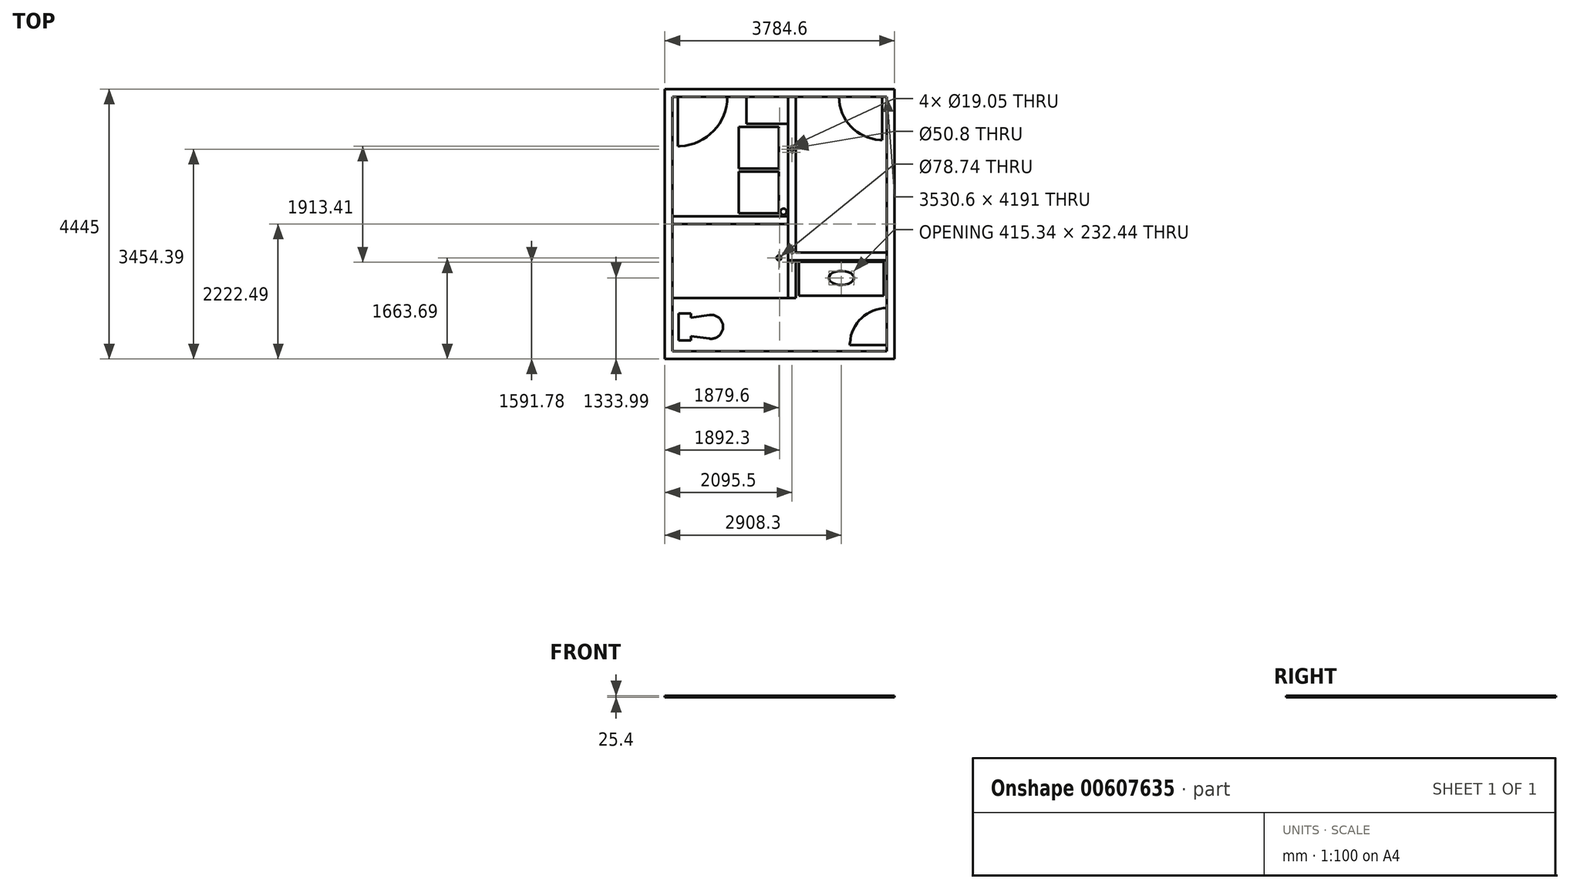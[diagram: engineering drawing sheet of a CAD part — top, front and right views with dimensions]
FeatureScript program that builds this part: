
annotation { "Feature Type Name" : "Feature", "Feature Type Description" : "" }
export const myFeature = defineFeature(function(context is Context, id is Id, definition is map)
    precondition{}
    {
        {
            var Q0;
            Q0=qCreatedBy(makeId("Top.planeOp"),FACE);
            var sketch = newSketch(context, id + "F0", { "sketchPlane" : qUnion([Q0])});
            skLineSegment(sketch, "E0.bottom", {"start": v(-1822.2, 1899.12) * mm, "end": v(1708.4, 1899.12) * mm, "construction": true});
            skLineSegment(sketch, "E0.top", {"start": v(-1822.2, -2291.88) * mm, "end": v(1708.4, -2291.88) * mm, "construction": true});
            skLineSegment(sketch, "E0.left", {"start": v(-1822.2, 1899.12) * mm, "end": v(-1822.2, -2291.88) * mm, "construction": true});
            skLineSegment(sketch, "E0.right", {"start": v(1708.4, 1899.12) * mm, "end": v(1708.4, -2291.88) * mm, "construction": true});
            skLineSegment(sketch, "E1.bottom", {"start": v(-1822.2, 1899.12) * mm, "end": v(1708.4, 1899.12) * mm});
            skLineSegment(sketch, "E1.top", {"start": v(-1822.2, -2291.88) * mm, "end": v(1708.4, -2291.88) * mm});
            skLineSegment(sketch, "E1.left", {"start": v(-1822.2, 1899.12) * mm, "end": v(-1822.2, -2291.88) * mm});
            skLineSegment(sketch, "E1.right", {"start": v(1708.4, 1899.12) * mm, "end": v(1708.4, -2291.88) * mm});
            skLineSegment(sketch, "E2", {"start": v(-1949.2, 2026.12) * mm, "end": v(1835.4, 2026.12) * mm});
            skLineSegment(sketch, "E3", {"start": v(1835.4, 2026.12) * mm, "end": v(1835.4, -2418.88) * mm});
            skLineSegment(sketch, "E4", {"start": v(1835.4, -2418.88) * mm, "end": v(-1949.2, -2418.88) * mm});
            skLineSegment(sketch, "E5", {"start": v(-1949.2, -2418.88) * mm, "end": v(-1949.2, 2026.12) * mm});
            skSolve(sketch);
        }
        {
            var Q0;
            Q0=qCreatedBy(makeId("Top.planeOp"),FACE);
            var sketch = newSketch(context, id + "F1", { "sketchPlane" : qUnion([Q0])});
            skLineSegment(sketch, "E6.bottom", {"start": v(-603, 1899.12) * mm, "end": v(82.8, 1899.12) * mm});
            skLineSegment(sketch, "E6.top", {"start": v(-603, 1454.62) * mm, "end": v(82.8, 1454.62) * mm});
            skLineSegment(sketch, "E6.left", {"start": v(-603, 1899.12) * mm, "end": v(-603, 1454.62) * mm});
            skLineSegment(sketch, "E6.right", {"start": v(82.8, 1899.12) * mm, "end": v(82.8, 1454.62) * mm});
            skSolve(sketch);
        }
        {
            var Q0;
            Q0=qCreatedBy(makeId("Top.planeOp"),FACE);
            var sketch = newSketch(context, id + "F2", { "sketchPlane" : qUnion([Q0])});
            skLineSegment(sketch, "E7.bottom", {"start": v(1708.4, -793.28) * mm, "end": v(82.8, -793.28) * mm});
            skLineSegment(sketch, "E7.top", {"start": v(1708.4, -666.28) * mm, "end": v(82.8, -666.28) * mm});
            skLineSegment(sketch, "E7.left", {"start": v(1708.4, -793.28) * mm, "end": v(1708.4, -666.28) * mm});
            skLineSegment(sketch, "E7.right", {"start": v(82.8, -793.28) * mm, "end": v(82.8, -666.28) * mm});
            skLineSegment(sketch, "E8.bottom", {"start": v(82.8, -666.28) * mm, "end": v(209.8, -666.28) * mm});
            skLineSegment(sketch, "E8.top", {"start": v(82.8, 1899.12) * mm, "end": v(209.8, 1899.12) * mm});
            skLineSegment(sketch, "E8.left", {"start": v(82.8, -666.28) * mm, "end": v(82.8, 1899.12) * mm});
            skLineSegment(sketch, "E8.right", {"start": v(209.8, -666.28) * mm, "end": v(209.8, 1899.12) * mm});
            skSolve(sketch);
        }
        {
            var Q0;
            Q0=qCreatedBy(makeId("Top.planeOp"),FACE);
            var sketch = newSketch(context, id + "F3", { "sketchPlane" : qUnion([Q0])});
            skLineSegment(sketch, "E9.bottom", {"start": v(1098.8, -2152.18) * mm, "end": v(1708.4, -2152.18) * mm});
            skLineSegment(sketch, "E9.top", {"start": v(1098.8, -2190.28) * mm, "end": v(1708.4, -2190.28) * mm});
            skLineSegment(sketch, "E9.left", {"start": v(1098.8, -2190.28) * mm, "end": v(1098.8, -2152.18) * mm});
            skLineSegment(sketch, "E9.right", {"start": v(1708.4, -2190.28) * mm, "end": v(1708.4, -2152.18) * mm});
            skArc(sketch, "E10", {"start": v(1098.8, -2190.28) * mm, "mid": v(1277.35, -1759.23) * mm, "end": v(1708.4, -1580.68) * mm});
            skLineSegment(sketch, "E11", {"start": v(1708.4, -1580.68) * mm, "end": v(1708.4, -2152.18) * mm});
            skSolve(sketch);
        }
        {
            var Q0;
            Q0=qCreatedBy(makeId("Top.planeOp"),FACE);
            var sketch = newSketch(context, id + "F4", { "sketchPlane" : qUnion([Q0])});
            skLineSegment(sketch, "E12.bottom", {"start": v(1632.2, 1899.12) * mm, "end": v(1594.1, 1899.12) * mm});
            skLineSegment(sketch, "E12.top", {"start": v(1632.2, 1187.92) * mm, "end": v(1594.1, 1187.92) * mm});
            skLineSegment(sketch, "E12.left", {"start": v(1632.2, 1899.12) * mm, "end": v(1632.2, 1187.92) * mm});
            skLineSegment(sketch, "E12.right", {"start": v(1594.1, 1899.12) * mm, "end": v(1594.1, 1187.92) * mm});
            skArc(sketch, "E13", {"start": v(1632.2, 1187.92) * mm, "mid": v(1129.3, 1396.22) * mm, "end": v(921, 1899.12) * mm});
            skLineSegment(sketch, "E14", {"start": v(921, 1899.12) * mm, "end": v(1594.1, 1899.12) * mm});
            skSolve(sketch);
        }
        {
            var Q0;
            Q0=qCreatedBy(makeId("Top.planeOp"),FACE);
            var sketch = newSketch(context, id + "F5", { "sketchPlane" : qUnion([Q0])});
            skLineSegment(sketch, "E15.bottom", {"start": v(-1733.3, 1899.12) * mm, "end": v(-1695.2, 1899.12) * mm});
            skLineSegment(sketch, "E15.top", {"start": v(-1733.3, 1086.32) * mm, "end": v(-1695.2, 1086.32) * mm});
            skLineSegment(sketch, "E15.left", {"start": v(-1733.3, 1899.12) * mm, "end": v(-1733.3, 1086.32) * mm});
            skLineSegment(sketch, "E15.right", {"start": v(-1695.2, 1899.12) * mm, "end": v(-1695.2, 1086.32) * mm});
            skArc(sketch, "E16", {"start": v(-1733.3, 1086.32) * mm, "mid": v(-1158.56, 1324.38) * mm, "end": v(-920.5, 1899.12) * mm});
            skLineSegment(sketch, "E17", {"start": v(-1695.2, 1899.12) * mm, "end": v(-920.5, 1899.12) * mm});
            skSolve(sketch);
        }
        {
            var Q0;
            Q0=qCreatedBy(makeId("Top.planeOp"),FACE);
            var sketch = newSketch(context, id + "F6", { "sketchPlane" : qUnion([Q0])});
            skLineSegment(sketch, "E18.bottom", {"start": v(-1822.2, -69.38) * mm, "end": v(82.8, -69.38) * mm});
            skLineSegment(sketch, "E18.top", {"start": v(-1822.2, -196.38) * mm, "end": v(82.8, -196.38) * mm});
            skLineSegment(sketch, "E18.left", {"start": v(-1822.2, -69.38) * mm, "end": v(-1822.2, -196.38) * mm});
            skLineSegment(sketch, "E18.right", {"start": v(82.8, -69.38) * mm, "end": v(82.8, -196.38) * mm});
            skSolve(sketch);
        }
        {
            var Q0;
            Q0=qCreatedBy(makeId("Top.planeOp"),FACE);
            var sketch = newSketch(context, id + "F7", { "sketchPlane" : qUnion([Q0])});
            skLineSegment(sketch, "E19.bottom", {"start": v(-730, 1403.82) * mm, "end": v(-69.6, 1403.82) * mm});
            skLineSegment(sketch, "E19.top", {"start": v(-730, 718.02) * mm, "end": v(-69.6, 718.02) * mm});
            skLineSegment(sketch, "E19.left", {"start": v(-730, 1403.82) * mm, "end": v(-730, 718.02) * mm});
            skLineSegment(sketch, "E19.right", {"start": v(-69.6, 1403.82) * mm, "end": v(-69.6, 718.02) * mm});
            skSolve(sketch);
        }
        {
            var Q0;
            Q0=qCreatedBy(makeId("Top.planeOp"),FACE);
            var sketch = newSketch(context, id + "F8", { "sketchPlane" : qUnion([Q0])});
            skLineSegment(sketch, "E20.bottom", {"start": v(-730, 667.22) * mm, "end": v(-69.6, 667.22) * mm});
            skLineSegment(sketch, "E20.top", {"start": v(-730, -18.58) * mm, "end": v(-69.6, -18.58) * mm});
            skLineSegment(sketch, "E20.left", {"start": v(-730, 667.22) * mm, "end": v(-730, -18.58) * mm});
            skLineSegment(sketch, "E20.right", {"start": v(-69.6, 667.22) * mm, "end": v(-69.6, -18.58) * mm});
            skSolve(sketch);
        }
        {
            var Q0;
            Q0=qCreatedBy(makeId("Top.planeOp"),FACE);
            var sketch = newSketch(context, id + "F9", { "sketchPlane" : qUnion([Q0])});
            skCircle(sketch, "E21", {"center": v(6.6, 6.82) * mm, "radius": 50.8 * mm});
            skSolve(sketch);
        }
        {
            var Q0;
            Q0=qCreatedBy(makeId("Top.planeOp"),FACE);
            var sketch = newSketch(context, id + "F10", { "sketchPlane" : qUnion([Q0])});
            skCircle(sketch, "E22", {"center": v(146.3, 1035.52) * mm, "radius": 25.4 * mm});
            skCircle(sketch, "E23", {"center": v(146.3, 1086.32) * mm, "radius": 9.53 * mm});
            skCircle(sketch, "E24", {"center": v(146.3, 984.72) * mm, "radius": 9.53 * mm});
            skSolve(sketch);
        }
        {
            var Q0;
            Q0=qCreatedBy(makeId("Top.planeOp"),FACE);
            var sketch = newSketch(context, id + "F11", { "sketchPlane" : qUnion([Q0])});
            skLineSegment(sketch, "E25.bottom", {"start": v(-1822.2, -196.38) * mm, "end": v(82.8, -196.38) * mm});
            skLineSegment(sketch, "E25.top", {"start": v(-1822.2, -1415.58) * mm, "end": v(82.8, -1415.58) * mm});
            skLineSegment(sketch, "E25.left", {"start": v(-1822.2, -196.38) * mm, "end": v(-1822.2, -1415.58) * mm});
            skLineSegment(sketch, "E25.right", {"start": v(82.8, -196.38) * mm, "end": v(82.8, -1415.58) * mm});
            skLineSegment(sketch, "E26.bottom", {"start": v(-1720.6, -1667.08) * mm, "end": v(-1517.6, -1667.08) * mm});
            skLineSegment(sketch, "E26.top", {"start": v(-1720.6, -2114.08) * mm, "end": v(-1517.6, -2114.08) * mm});
            skLineSegment(sketch, "E26.left", {"start": v(-1720.6, -1667.08) * mm, "end": v(-1720.6, -2114.08) * mm});
            skLineSegment(sketch, "E26.right", {"start": v(-1517.6, -1667.08) * mm, "end": v(-1517.6, -2114.08) * mm});
            skPoint(sketch, "E27.endSnap0", {"position": v(-1517.6, -1890.58) * mm});
            skLineSegment(sketch, "E28", {"start": v(-1517.6, -1738.18) * mm, "end": v(-1214.28, -1695.91) * mm});
            skLineSegment(sketch, "E29", {"start": v(-1517.6, -2042.98) * mm, "end": v(-1214.28, -2085.26) * mm});
            skArc(sketch, "E30", {"start": v(-990.6, -1890.58) * mm, "mid": v(-1058.12, -1742.32) * mm, "end": v(-1214.28, -1695.91) * mm});
            skArc(sketch, "E31", {"start": v(-1214.28, -2085.26) * mm, "mid": v(-1058.12, -2038.85) * mm, "end": v(-990.6, -1890.58) * mm});
            skSolve(sketch);
        }
        {
            var Q0;
            Q0=qCreatedBy(makeId("Top.planeOp"),FACE);
            var sketch = newSketch(context, id + "F12", { "sketchPlane" : qUnion([Q0])});
            skLineSegment(sketch, "E32.bottom", {"start": v(82.8, -793.28) * mm, "end": v(209.8, -793.28) * mm});
            skLineSegment(sketch, "E32.top", {"start": v(82.8, -1415.58) * mm, "end": v(209.8, -1415.58) * mm});
            skLineSegment(sketch, "E32.left", {"start": v(82.8, -793.28) * mm, "end": v(82.8, -1415.58) * mm});
            skLineSegment(sketch, "E32.right", {"start": v(209.8, -793.28) * mm, "end": v(209.8, -1415.58) * mm});
            skSolve(sketch);
        }
        {
            var Q0;
            Q0=qCreatedBy(makeId("Top.planeOp"),FACE);
            var sketch = newSketch(context, id + "F13", { "sketchPlane" : qUnion([Q0])});
            skCircle(sketch, "E33", {"center": v(-69.6, -755.18) * mm, "radius": 39.37 * mm});
            skCircle(sketch, "E34", {"center": v(146.3, -827.1) * mm, "radius": 9.53 * mm});
            skCircle(sketch, "E35", {"center": v(146.3, -674.7) * mm, "radius": 9.53 * mm});
            skSolve(sketch);
        }
        {
            var Q0;
            Q0=qCreatedBy(makeId("Top.planeOp"),FACE);
            var sketch = newSketch(context, id + "F14", { "sketchPlane" : qUnion([Q0])});
            skLineSegment(sketch, "E36.bottom", {"start": v(260.6, -1377.48) * mm, "end": v(1657.6, -1377.48) * mm});
            skLineSegment(sketch, "E36.top", {"start": v(260.6, -818.68) * mm, "end": v(1657.6, -818.68) * mm});
            skLineSegment(sketch, "E36.left", {"start": v(260.6, -1377.48) * mm, "end": v(260.6, -818.68) * mm});
            skLineSegment(sketch, "E36.right", {"start": v(1657.6, -1377.48) * mm, "end": v(1657.6, -818.68) * mm});
            skEllipse(sketch, "E37", {"center": v(959.1, -1084.9) * mm, "majorRadius": 207.67 * mm, "minorRadius": 116.22 * mm, "majorAxis": v(-1, 0)});
            skSolve(sketch);
        }
        {
            var Q0;
            Q0 = qSketchRegion(id + "F1", true);
            var Q1;
            Q1 = qSketchRegion(id + "F2", true);
            var Q2;
            Q2 = qSketchRegion(id + "F4", true);
            var Q3;
            Q3 = qSketchRegion(id + "F3", true);
            var Q4;
            Q4 = qSketchRegion(id + "F5", true);
            var Q5;
            Q5=makeQuery(id+"F0.imprint","IMPRINT",FACE,{"disambiguationData":[TD([[makeQuery(id+"F0.imprint","IMPRINT",EDGE,{"derivedFrom":sQuery(id+"F0.wireOp",EDGE,"E1.bottom")}),1.0]])]});
            var Q6;
            Q6 = qSketchRegion(id + "F6", true);
            var Q7;
            Q7 = qSketchRegion(id + "F7", true);
            var Q8;
            Q8 = qSketchRegion(id + "F8", true);
            var Q9;
            Q9 = qSketchRegion(id + "F9", true);
            var Q10;
            Q10 = qSketchRegion(id + "F13", true);
            var Q11;
            Q11 = qSketchRegion(id + "F10", true);
            var Q12;
            Q12 = qSketchRegion(id + "F11", true);
            var Q13;
            Q13 = qSketchRegion(id + "F12", true);
            var Q14;
            Q14 = qSketchRegion(id + "F14", true);
            extrude(context, id + "F15", {"entities" : qUnion([Q0, Q1, Q2, Q3, Q4, Q5, Q6, Q7, Q8, Q9, Q10, Q11, Q12, Q13, Q14]), "depth" : 25.4 * mm, "offsetDistance" : 25.4 * mm});
        }
        {
            var Q0;
            Q0=makeQuery(id+"F15.opExtrude","SWEPT_BODY",BODY,{"disambiguationData":[OSD([sQuery(id+"F10.wireOp",EDGE,"E23")])]});
            var Q1;
            Q1=makeQuery(id+"F15.opExtrude","SWEPT_BODY",BODY,{"disambiguationData":[OSD([sQuery(id+"F10.wireOp",EDGE,"E22")])]});
            var Q2;
            Q2=makeQuery(id+"F15.opExtrude","SWEPT_BODY",BODY,{"disambiguationData":[OSD([sQuery(id+"F10.wireOp",EDGE,"E24")])]});
            var Q3;
            Q3=makeQuery(id+"F15.opExtrude","SWEPT_BODY",BODY,{"disambiguationData":[OSD([sQuery(id+"F13.wireOp",EDGE,"E35")])]});
            var Q4;
            Q4=makeQuery(id+"F15.opExtrude","SWEPT_BODY",BODY,{"disambiguationData":[OSD([sQuery(id+"F13.wireOp",EDGE,"E34")])]});
            var Q5;
            Q5=makeQuery(id+"F15.opExtrude","SWEPT_BODY",BODY,{"disambiguationData":[OSD([sQuery(id+"F13.wireOp",EDGE,"E33")])]});
            var Q6;
            Q6=makeQuery(id+"F15.opExtrude","SWEPT_BODY",BODY,{"disambiguationData":[OSD([sQuery(id+"F2.wireOp",EDGE,"E7.bottom"),sQuery(id+"F2.wireOp",EDGE,"E7.top"),sQuery(id+"F2.wireOp",EDGE,"E7.left"),sQuery(id+"F2.wireOp",EDGE,"E7.right"),sQuery(id+"F2.wireOp",EDGE,"E8.top"),sQuery(id+"F2.wireOp",EDGE,"E8.left"),sQuery(id+"F2.wireOp",EDGE,"E8.right")])]});
            var Q7;
            Q7=makeQuery(id+"F15.opExtrude","SWEPT_BODY",BODY,{"disambiguationData":[OSD([sQuery(id+"F12.wireOp",EDGE,"E32.bottom"),sQuery(id+"F12.wireOp",EDGE,"E32.top"),sQuery(id+"F12.wireOp",EDGE,"E32.left"),sQuery(id+"F12.wireOp",EDGE,"E32.right")])]});
            var Q8;
            Q8=makeQuery(id+"F15.opExtrude","SWEPT_BODY",BODY,{"disambiguationData":[OSD([sQuery(id+"F11.wireOp",EDGE,"E25.bottom"),sQuery(id+"F11.wireOp",EDGE,"E25.top"),sQuery(id+"F11.wireOp",EDGE,"E25.left"),sQuery(id+"F11.wireOp",EDGE,"E25.right")])]});
            booleanBodies(context, id + "F16", {"operationType" : BooleanOperationType.SUBTRACTION, "tools" : qUnion([Q0, Q1, Q2, Q3, Q4, Q5]), "targets" : qUnion([Q6, Q7, Q8])});
        }
    });
